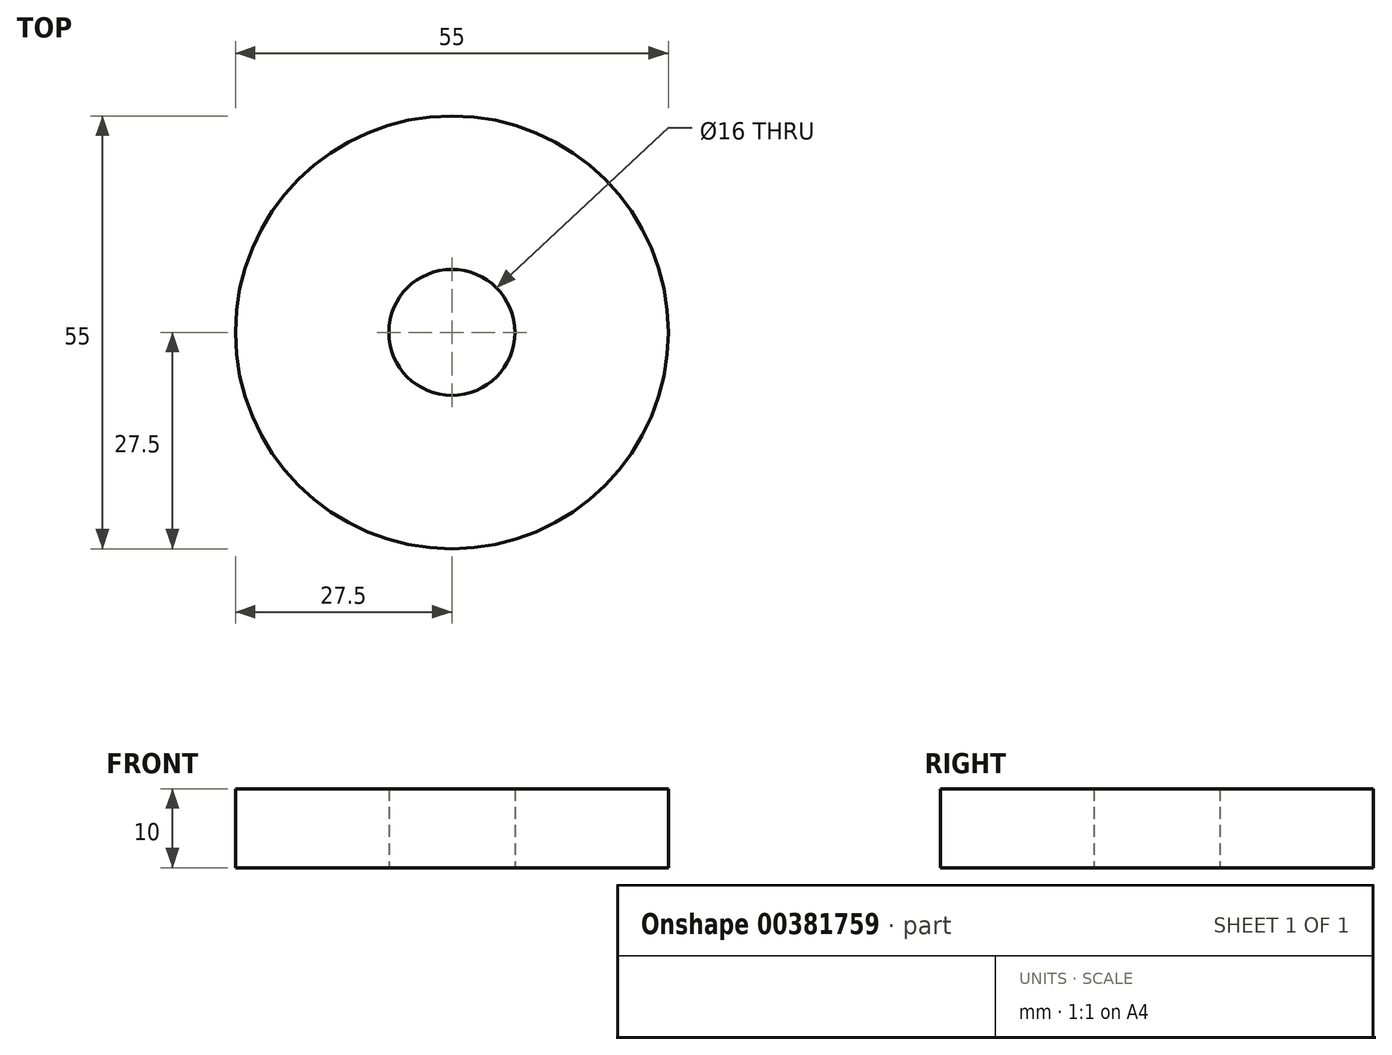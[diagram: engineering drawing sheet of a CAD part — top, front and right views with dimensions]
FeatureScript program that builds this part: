
annotation { "Feature Type Name" : "Feature", "Feature Type Description" : "" }
export const myFeature = defineFeature(function(context is Context, id is Id, definition is map)
    precondition{}
    {
        {
            var Q0;
            Q0=qCreatedBy(makeId("Top.planeOp"),FACE);
            var sketch = newSketch(context, id + "F0", { "sketchPlane" : qUnion([Q0])});
            skCircle(sketch, "E0", {"center": v(0, 0) * mm, "radius": 8 * mm});
            skCircle(sketch, "E1", {"center": v(0, 0) * mm, "radius": 27.5 * mm});
            skSolve(sketch);
        }
        {
            var Q0;
            Q0=makeQuery(id+"F0.imprint","IMPRINT",FACE,{"disambiguationData":[TD([[makeQuery(id+"F0.imprint","IMPRINT",EDGE,{"derivedFrom":sQuery(id+"F0.wireOp",EDGE,"E0")}),-1.0]])]});
            extrude(context, id + "F1", {"entities" : qUnion([Q0]), "depth" : 10 * mm});
        }
    });
